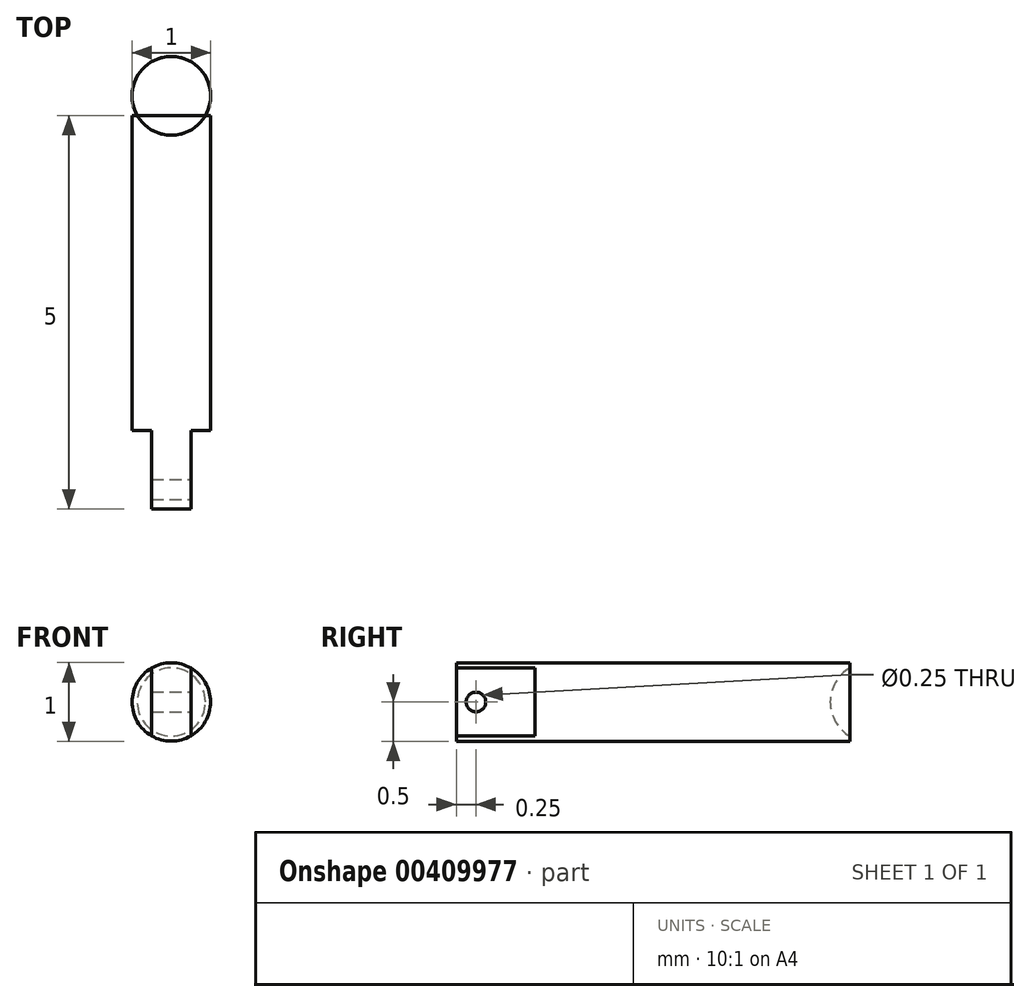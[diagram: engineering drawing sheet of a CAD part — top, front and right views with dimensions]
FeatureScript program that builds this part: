
annotation { "Feature Type Name" : "Feature", "Feature Type Description" : "" }
export const myFeature = defineFeature(function(context is Context, id is Id, definition is map)
    precondition{}
    {
        {
            var Q0;
            Q0=qCreatedBy(makeId("Front.planeOp"),FACE);
            var sketch = newSketch(context, id + "F0", { "sketchPlane" : qUnion([Q0])});
            skCircle(sketch, "E0", {"center": v(0, 0) * mm, "radius": 0.5 * mm});
            skSolve(sketch);
        }
        {
            var Q0;
            Q0=makeQuery(id+"F0.imprint","IMPRINT",FACE,{"disambiguationData":[TD([[makeQuery(id+"F0.imprint","IMPRINT",EDGE,{"derivedFrom":sQuery(id+"F0.wireOp",EDGE,"E0")}),1.0]])]});
            extrude(context, id + "F1", {"entities" : qUnion([Q0]), "depth" : 5 * mm});
        }
        {
            var Q0;
            Q0=makeQuery(id+"F1.opExtrude","CAP_FACE",FACE,{"disambiguationData":[OSD([sQuery(id+"F0.wireOp",EDGE,"E0")])],"isStart":false});
            var sketch = newSketch(context, id + "F2", { "sketchPlane" : qUnion([Q0])});
            skLineSegment(sketch, "E1.bottom", {"start": v(-0.95, 0.85) * mm, "end": v(-0.25, 0.85) * mm});
            skLineSegment(sketch, "E1.top", {"start": v(-0.95, -0.82) * mm, "end": v(-0.25, -0.82) * mm});
            skLineSegment(sketch, "E1.left", {"start": v(-0.95, 0.85) * mm, "end": v(-0.95, -0.82) * mm});
            skLineSegment(sketch, "E1.right", {"start": v(-0.25, 0.85) * mm, "end": v(-0.25, -0.82) * mm});
            skSolve(sketch);
        }
        {
            var Q0;
            Q0 = qSketchRegion(id + "F2", true);
            extrude(context, id + "F3", {"entities" : qUnion([Q0]), "operationType" : NewBodyOperationType.REMOVE, "oppositeDirection" : true, "depth" : 1 * mm});
        }
        {
            var Q0;
            Q0=makeQuery(id+"F1.opExtrude","CAP_FACE",FACE,{"disambiguationData":[OSD([sQuery(id+"F0.wireOp",EDGE,"E0")])],"isStart":false});
            var sketch = newSketch(context, id + "F4", { "sketchPlane" : qUnion([Q0])});
            skLineSegment(sketch, "E2.bottom", {"start": v(0.25, 0.6) * mm, "end": v(0.74, 0.6) * mm});
            skLineSegment(sketch, "E2.top", {"start": v(0.25, -0.82) * mm, "end": v(0.74, -0.82) * mm});
            skLineSegment(sketch, "E2.left", {"start": v(0.25, 0.6) * mm, "end": v(0.25, -0.82) * mm});
            skLineSegment(sketch, "E2.right", {"start": v(0.74, 0.6) * mm, "end": v(0.74, -0.82) * mm});
            skSolve(sketch);
        }
        {
            var Q0;
            Q0 = qSketchRegion(id + "F4", true);
            extrude(context, id + "F5", {"entities" : qUnion([Q0]), "operationType" : NewBodyOperationType.REMOVE, "oppositeDirection" : true, "depth" : 1 * mm});
        }
        {
            var Q0;
            Q0=makeQuery(id+"F5.boolean.opBoolean","COPY",FACE,{"derivedFrom":makeQuery(id+"F5.opExtrude","SWEPT_FACE",FACE,{"disambiguationData":[OSD([sQuery(id+"F4.wireOp",EDGE,"E2.left")])]})});
            var sketch = newSketch(context, id + "F6", { "sketchPlane" : qUnion([Q0])});
            skCircle(sketch, "E3", {"center": v(-4.75, 0) * mm, "radius": 0.12 * mm});
            skSolve(sketch);
        }
        {
            var Q0;
            Q0=makeQuery(id+"F6.imprint","IMPRINT",FACE,{"disambiguationData":[TD([[makeQuery(id+"F6.imprint","IMPRINT",EDGE,{"derivedFrom":sQuery(id+"F6.wireOp",EDGE,"E3")}),1.0]])]});
            extrude(context, id + "F7", {"entities" : qUnion([Q0]), "operationType" : NewBodyOperationType.REMOVE, "oppositeDirection" : true, "depth" : 25 * mm});
        }
        {
            var Q0;
            Q0=qCreatedBy(makeId("Right.planeOp"),FACE);
            var sketch = newSketch(context, id + "F8", { "sketchPlane" : qUnion([Q0])});
            skArc(sketch, "E4", {"start": v(0.25, 0.5) * mm, "mid": v(-0.25, 0) * mm, "end": v(0.25, -0.5) * mm});
            skLineSegment(sketch, "E5", {"start": v(0.25, -0.5) * mm, "end": v(0.25, 0.5) * mm});
            skPoint(sketch, "E6.orphan", {"position": v(0.25, -0.54) * mm});
            skSolve(sketch);
        }
        {
            var Q0;
            Q0=makeQuery(id+"F8.imprint","IMPRINT",FACE,{"disambiguationData":[TD([[makeQuery(id+"F8.imprint","IMPRINT",EDGE,{"derivedFrom":sQuery(id+"F8.wireOp",EDGE,"E4")}),1.0]])]});
            var Q1;
            Q1=sQuery(id+"F8.wireOp",EDGE,"E5");
            revolve(context, id + "F9", {"operationType" : NewBodyOperationType.REMOVE, "entities" : qUnion([Q0]), "axis" : qUnion([Q1]), "revolveType" : RevolveType.FULL, "oppositeDirection" : true});
        }
    });
